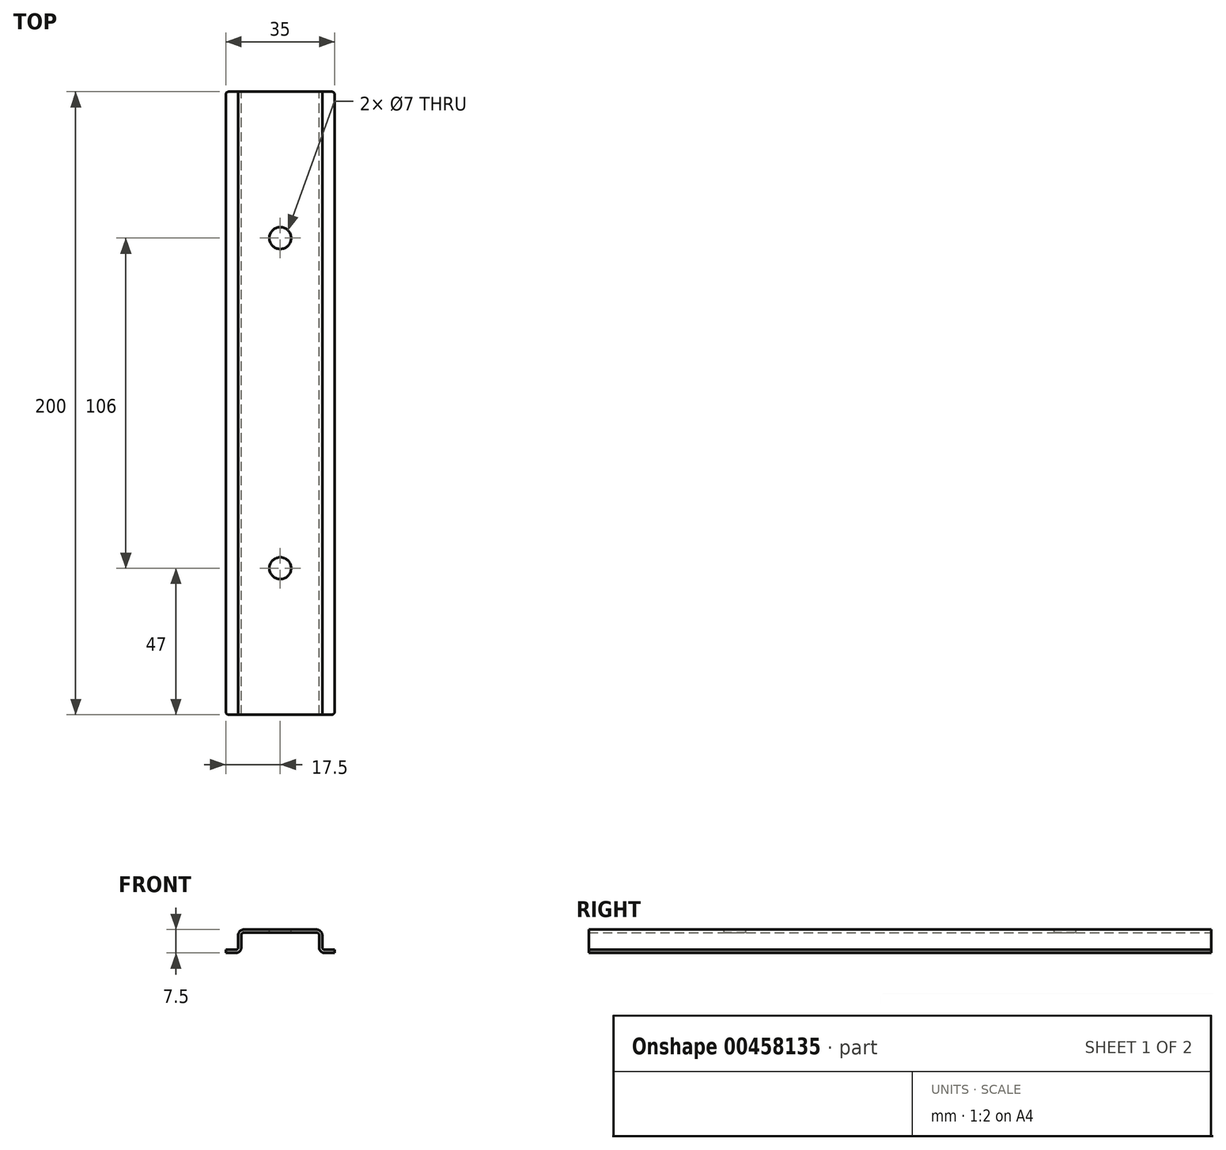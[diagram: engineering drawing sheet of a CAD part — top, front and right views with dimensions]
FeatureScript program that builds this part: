
annotation { "Feature Type Name" : "Feature", "Feature Type Description" : "" }
export const myFeature = defineFeature(function(context is Context, id is Id, definition is map)
    precondition{}
    {
        {
            var Q0;
            Q0=qCreatedBy(makeId("Front.planeOp"),FACE);
            var sketch = newSketch(context, id + "F0", { "sketchPlane" : qUnion([Q0])});
            skLineSegment(sketch, "E0", {"start": v(0, 0) * mm, "end": v(0, 7.5) * mm, "construction": true});
            skLineSegment(sketch, "E1", {"start": v(0, 7.5) * mm, "end": v(-11.7, 7.5) * mm});
            skLineSegment(sketch, "E2", {"start": v(-13.5, 5.7) * mm, "end": v(-13.5, 1.8) * mm});
            skLineSegment(sketch, "E3", {"start": v(-14.3, 1) * mm, "end": v(-17.5, 1) * mm});
            skLineSegment(sketch, "E4", {"start": v(-17.5, 1) * mm, "end": v(-17.5, 0) * mm});
            skLineSegment(sketch, "E5", {"start": v(-17.5, 0) * mm, "end": v(-14.3, 0) * mm});
            skLineSegment(sketch, "E6", {"start": v(-12.5, 1.8) * mm, "end": v(-12.5, 5.7) * mm});
            skLineSegment(sketch, "E7", {"start": v(-11.7, 6.5) * mm, "end": v(0, 6.5) * mm});
            skLineSegment(sketch, "E8.MirrorCS", {"start": v(17.5, 1) * mm, "end": v(17.5, 0) * mm});
            skLineSegment(sketch, "E9.MirrorCS", {"start": v(0, 7.5) * mm, "end": v(11.7, 7.5) * mm});
            skLineSegment(sketch, "E10.MirrorCS", {"start": v(13.5, 5.7) * mm, "end": v(13.5, 1.8) * mm});
            skLineSegment(sketch, "E11.MirrorCS", {"start": v(17.5, 0) * mm, "end": v(14.3, 0) * mm});
            skLineSegment(sketch, "E12.MirrorCS", {"start": v(12.5, 1.8) * mm, "end": v(12.5, 5.7) * mm});
            skLineSegment(sketch, "E13.MirrorCS", {"start": v(14.3, 1) * mm, "end": v(17.5, 1) * mm});
            skLineSegment(sketch, "E14.MirrorCS", {"start": v(11.7, 6.5) * mm, "end": v(0, 6.5) * mm});
            skPoint(sketch, "E15.visualSharp", {"position": v(-12.5, 6.5) * mm});
            skArc(sketch, "E15.filletArc", {"start": v(-11.7, 6.5) * mm, "mid": v(-12.27, 6.27) * mm, "end": v(-12.5, 5.7) * mm});
            skPoint(sketch, "E16.visualSharp", {"position": v(12.5, 6.5) * mm});
            skArc(sketch, "E16.filletArc", {"start": v(12.5, 5.7) * mm, "mid": v(12.27, 6.27) * mm, "end": v(11.7, 6.5) * mm});
            skPoint(sketch, "E17.visualSharp", {"position": v(13.5, 1) * mm});
            skArc(sketch, "E17.filletArc", {"start": v(13.5, 1.8) * mm, "mid": v(13.73, 1.23) * mm, "end": v(14.3, 1) * mm});
            skPoint(sketch, "E18.visualSharp", {"position": v(-13.5, 1) * mm});
            skArc(sketch, "E18.filletArc", {"start": v(-14.3, 1) * mm, "mid": v(-13.73, 1.23) * mm, "end": v(-13.5, 1.8) * mm});
            skPoint(sketch, "E19.visualSharp", {"position": v(-13.5, 7.5) * mm});
            skArc(sketch, "E19.filletArc", {"start": v(-11.7, 7.5) * mm, "mid": v(-12.97, 6.97) * mm, "end": v(-13.5, 5.7) * mm});
            skPoint(sketch, "E20.visualSharp", {"position": v(13.5, 7.5) * mm});
            skArc(sketch, "E20.filletArc", {"start": v(13.5, 5.7) * mm, "mid": v(12.97, 6.97) * mm, "end": v(11.7, 7.5) * mm});
            skPoint(sketch, "E21.visualSharp", {"position": v(12.5, 0) * mm});
            skArc(sketch, "E21.filletArc", {"start": v(12.5, 1.8) * mm, "mid": v(13.03, 0.53) * mm, "end": v(14.3, 0) * mm});
            skPoint(sketch, "E22.visualSharp", {"position": v(-12.5, 0) * mm});
            skArc(sketch, "E22.filletArc", {"start": v(-14.3, 0) * mm, "mid": v(-13.03, 0.53) * mm, "end": v(-12.5, 1.8) * mm});
            skSolve(sketch);
        }
        {
            var Q0;
            Q0=qSketchRegion(id+"F0",true);
            extrude(context, id + "F1", {"entities" : qUnion([Q0]), "depth" : 200 * mm, "symmetric" : true});
        }
        {
            var Q0;
            Q0=makeQuery(id+"F1.opExtrude","SWEPT_FACE",FACE,{"disambiguationData":[OSD([sQuery(id+"F0.wireOp",EDGE,"E1"),sQuery(id+"F0.wireOp",EDGE,"E9.MirrorCS")])]});
            var sketch = newSketch(context, id + "F2", { "sketchPlane" : qUnion([Q0])});
            skCircle(sketch, "E23", {"center": v(0, 53) * mm, "radius": 3.5 * mm});
            skPoint(sketch, "E23.centerSnap0", {"position": v(0, 100) * mm});
            skCircle(sketch, "E24", {"center": v(0, -53) * mm, "radius": 3.5 * mm});
            skPoint(sketch, "E24.centerSnap0", {"position": v(0, -100) * mm});
            skSolve(sketch);
        }
        {
            var Q0;
            Q0=makeQuery(id+"F2.imprint","IMPRINT",FACE,{"disambiguationData":[TD([[makeQuery(id+"F2.imprint","IMPRINT",EDGE,{"derivedFrom":sQuery(id+"F2.wireOp",EDGE,"E23")}),1.0]])]});
            var Q1;
            Q1=makeQuery(id+"F2.imprint","IMPRINT",FACE,{"disambiguationData":[TD([[makeQuery(id+"F2.imprint","IMPRINT",EDGE,{"derivedFrom":sQuery(id+"F2.wireOp",EDGE,"E24")}),1.0]])]});
            extrude(context, id + "F3", {"entities" : qUnion([Q0, Q1]), "operationType" : NewBodyOperationType.REMOVE, "oppositeDirection" : true, "depth" : 25 * mm});
        }
        {
            var Q0;
            Q0=makeQuery(id+"F1.opExtrude","CAP_EDGE",EDGE,{"disambiguationData":[OSD([sQuery(id+"F0.wireOp",EDGE,"E8.MirrorCS")])],"isStart":true});
            var Q1;
            Q1=makeQuery(id+"F1.opExtrude","CAP_EDGE",EDGE,{"disambiguationData":[OSD([sQuery(id+"F0.wireOp",EDGE,"E4")])],"isStart":true});
            var Q2;
            Q2=makeQuery(id+"F1.opExtrude","CAP_EDGE",EDGE,{"disambiguationData":[OSD([sQuery(id+"F0.wireOp",EDGE,"E8.MirrorCS")])],"isStart":false});
            var Q3;
            Q3=makeQuery(id+"F1.opExtrude","CAP_EDGE",EDGE,{"disambiguationData":[OSD([sQuery(id+"F0.wireOp",EDGE,"E4")])],"isStart":false});
            fillet(context, id + "F4", {"entities" : qUnion([Q0, Q1, Q2, Q3]), "radius" : 1 * mm, "tangentPropagation" : true, "allowEdgeOverflow" : false});
        }
    });
